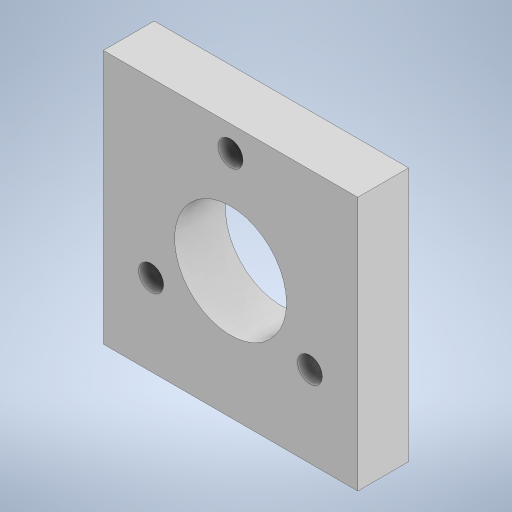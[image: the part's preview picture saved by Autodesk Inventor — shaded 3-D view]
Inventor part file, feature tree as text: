
AUTODESK INVENTOR PART (.ipt)
format: ipt  version: 2024 (Build 280153000, 153)  size: 226,304 bytes
history: native  units: in
note: dims shown in document units (in); Inventor stores cm internally (conversion verified against a paired STEP export)
features: extrude x1, sketch x1
ambient origin geometry x8: Origin, YZ Plane, XZ Plane, XY Plane, X Axis, Y Axis, Z Axis, Center Point
bodies: Body1 (feature_tree)
feature tree (2):
  extrude  "Extrusion2"  Depth=1.9685in
  sketch  "Sketch1"  dims[d0=1.9685in d1=1.9685in d2=0.8661in d3=0.7874in d4=0.6142in d5=120.0deg d6=0.6142in d7=120.0deg d8=0.1929in d9=0.1929in d10=0.1929in d16=0.3937in d17=0.0in d11=0.0197in d12=0.0344in d13=0.0197in d14=0.0344in]
